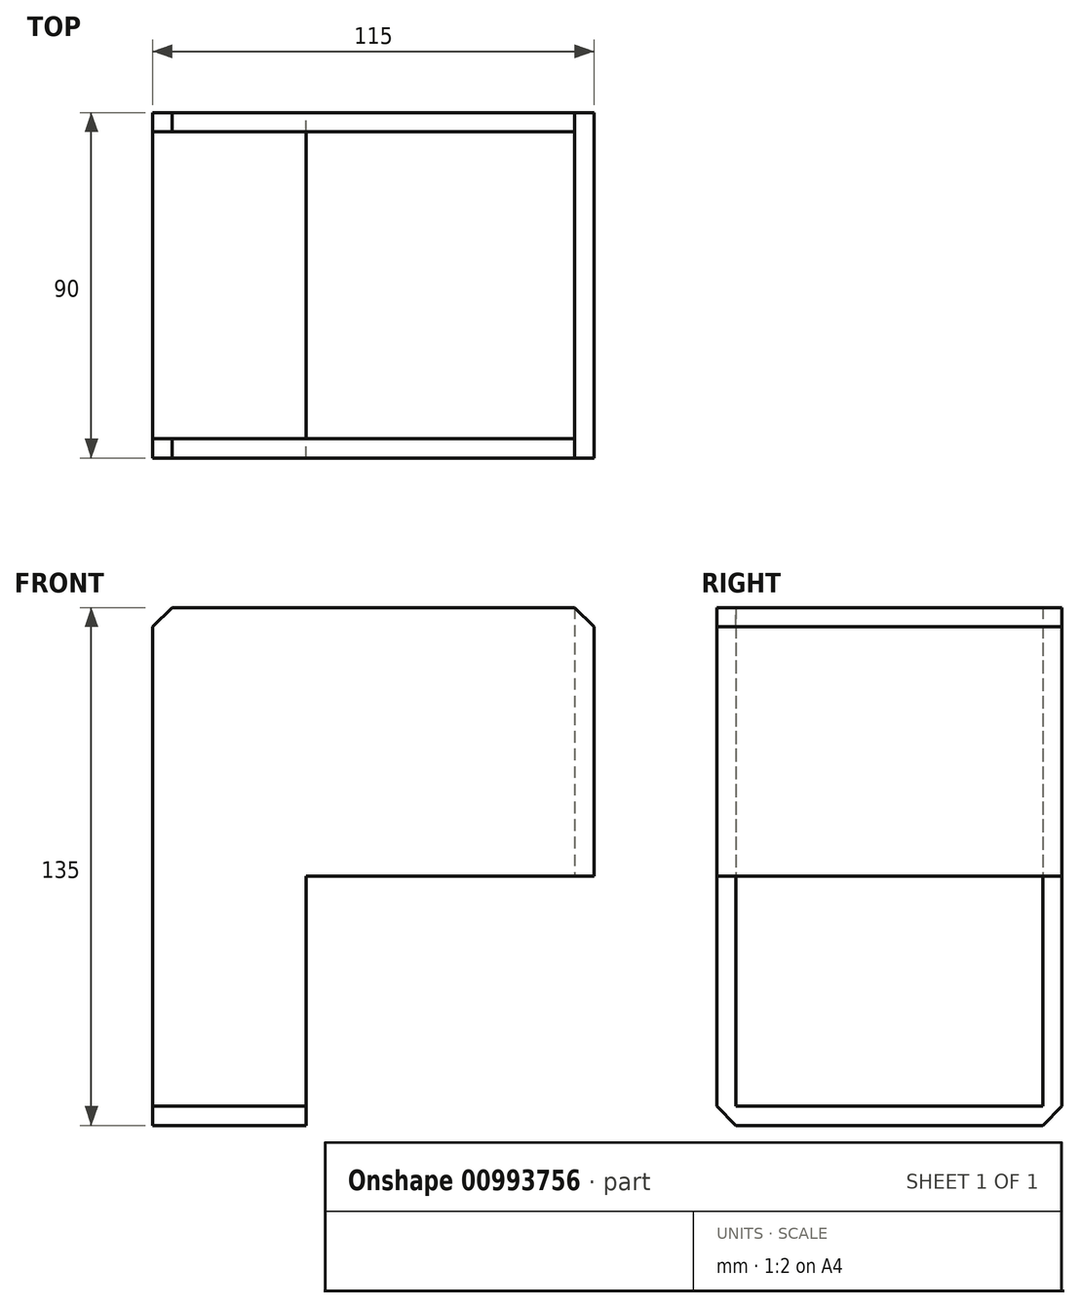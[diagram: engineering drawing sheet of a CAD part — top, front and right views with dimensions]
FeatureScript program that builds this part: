
annotation { "Feature Type Name" : "Feature", "Feature Type Description" : "" }
export const myFeature = defineFeature(function(context is Context, id is Id, definition is map)
    precondition{}
    {
        {
            var Q0;
            Q0=qCreatedBy(makeId("Right.planeOp"),FACE);
            var sketch = newSketch(context, id + "F0", { "sketchPlane" : qUnion([Q0])});
            skLineSegment(sketch, "E0.bottom", {"start": v(-45, 35) * mm, "end": v(45, 35) * mm});
            skLineSegment(sketch, "E0.top", {"start": v(-45, -35) * mm, "end": v(45, -35) * mm});
            skLineSegment(sketch, "E0.left", {"start": v(-45, 35) * mm, "end": v(-45, -35) * mm});
            skLineSegment(sketch, "E0.right", {"start": v(45, 35) * mm, "end": v(45, -35) * mm});
            skPoint(sketch, "E0.middle", {"position": v(0, 0) * mm});
            skSolve(sketch);
        }
        {
            var Q0;
            Q0=makeQuery(id+"F0.imprint","IMPRINT",FACE,{"disambiguationData":[TD([[makeQuery(id+"F0.imprint","IMPRINT",EDGE,{"derivedFrom":sQuery(id+"F0.wireOp",EDGE,"E0.bottom")}),-1.0]])]});
            extrude(context, id + "F1", {"entities" : qUnion([Q0]), "oppositeDirection" : true, "depth" : 5 * mm, "offsetDistance" : 25 * mm});
        }
        {
            var Q0;
            Q0=makeQuery(id+"F1.opExtrude","CAP_FACE",FACE,{"disambiguationData":[OSD([sQuery(id+"F0.wireOp",EDGE,"E0.bottom"),sQuery(id+"F0.wireOp",EDGE,"E0.top"),sQuery(id+"F0.wireOp",EDGE,"E0.left"),sQuery(id+"F0.wireOp",EDGE,"E0.right")])],"isStart":false});
            var sketch = newSketch(context, id + "F2", { "sketchPlane" : qUnion([Q0])});
            skLineSegment(sketch, "E1.bottom", {"start": v(-45, 35) * mm, "end": v(-40, 35) * mm});
            skLineSegment(sketch, "E1.top", {"start": v(-45, -35) * mm, "end": v(-40, -35) * mm});
            skLineSegment(sketch, "E1.left", {"start": v(-45, 35) * mm, "end": v(-45, -35) * mm});
            skLineSegment(sketch, "E1.right", {"start": v(-40, 35) * mm, "end": v(-40, -35) * mm});
            skLineSegment(sketch, "E2.bottom", {"start": v(45, 35) * mm, "end": v(40, 35) * mm});
            skLineSegment(sketch, "E2.top", {"start": v(45, -35) * mm, "end": v(40, -35) * mm});
            skLineSegment(sketch, "E2.left", {"start": v(45, 35) * mm, "end": v(45, -35) * mm});
            skLineSegment(sketch, "E2.right", {"start": v(40, 35) * mm, "end": v(40, -35) * mm});
            skSolve(sketch);
        }
        {
            var Q0;
            Q0 = qSketchRegion(id + "F2", true);
            extrude(context, id + "F3", {"entities" : qUnion([Q0]), "operationType" : NewBodyOperationType.ADD, "depth" : 110 * mm, "offsetDistance" : 25 * mm});
        }
        {
            var Q0;
            Q0=makeQuery(id+"F3.boolean.opBoolean","MERGE",FACE,{"derivedFrom":[makeQuery(id+"F1.opExtrude","SWEPT_FACE",FACE,{"disambiguationData":[OSD([sQuery(id+"F0.wireOp",EDGE,"E0.top")])]}),makeQuery(id+"F3.opExtrude","SWEPT_FACE",FACE,{"disambiguationData":[OSD([sQuery(id+"F2.wireOp",EDGE,"E1.top")])]}),makeQuery(id+"F3.opExtrude","SWEPT_FACE",FACE,{"disambiguationData":[OSD([sQuery(id+"F2.wireOp",EDGE,"E2.top")])]})]});
            var sketch = newSketch(context, id + "F4", { "sketchPlane" : qUnion([Q0])});
            skLineSegment(sketch, "E3.bottom", {"start": v(-115, 45) * mm, "end": v(-75, 45) * mm});
            skLineSegment(sketch, "E3.top", {"start": v(-115, 40) * mm, "end": v(-75, 40) * mm});
            skLineSegment(sketch, "E3.left", {"start": v(-115, 45) * mm, "end": v(-115, 40) * mm});
            skLineSegment(sketch, "E3.right", {"start": v(-75, 45) * mm, "end": v(-75, 40) * mm});
            skLineSegment(sketch, "E4.bottom", {"start": v(-115, -40) * mm, "end": v(-75, -40) * mm});
            skLineSegment(sketch, "E4.top", {"start": v(-115, -45) * mm, "end": v(-75, -45) * mm});
            skLineSegment(sketch, "E4.left", {"start": v(-115, -40) * mm, "end": v(-115, -45) * mm});
            skLineSegment(sketch, "E4.right", {"start": v(-75, -40) * mm, "end": v(-75, -45) * mm});
            skSolve(sketch);
        }
        {
            var Q0;
            Q0 = qSketchRegion(id + "F4", true);
            extrude(context, id + "F5", {"entities" : qUnion([Q0]), "operationType" : NewBodyOperationType.ADD, "depth" : 65 * mm, "offsetDistance" : 25 * mm});
        }
        {
            var Q0;
            Q0=makeQuery(id+"F5.boolean.opBoolean","MERGE",FACE,{"derivedFrom":[makeQuery(id+"F3.opExtrude","SWEPT_FACE",FACE,{"disambiguationData":[OSD([sQuery(id+"F2.wireOp",EDGE,"E2.right")])]}),makeQuery(id+"F5.opExtrude","SWEPT_FACE",FACE,{"disambiguationData":[OSD([sQuery(id+"F4.wireOp",EDGE,"E3.top")])]})]});
            var sketch = newSketch(context, id + "F6", { "sketchPlane" : qUnion([Q0])});
            skLineSegment(sketch, "E5.bottom", {"start": v(75, -100) * mm, "end": v(115, -100) * mm});
            skLineSegment(sketch, "E5.top", {"start": v(75, -95) * mm, "end": v(115, -95) * mm});
            skLineSegment(sketch, "E5.left", {"start": v(75, -100) * mm, "end": v(75, -95) * mm});
            skLineSegment(sketch, "E5.right", {"start": v(115, -100) * mm, "end": v(115, -95) * mm});
            skSolve(sketch);
        }
        {
            var Q0;
            Q0 = qSketchRegion(id + "F6", true);
            extrude(context, id + "F7", {"entities" : qUnion([Q0]), "operationType" : NewBodyOperationType.ADD, "endBound" : BoundingType.UP_TO_NEXT, "depth" : 25 * mm, "offsetDistance" : 25 * mm});
        }
        {
            var Q0;
            Q0=makeQuery(id+"F1.opExtrude","CAP_EDGE",EDGE,{"disambiguationData":[OSD([sQuery(id+"F0.wireOp",EDGE,"E0.bottom")])],"isStart":true});
            var Q1;
            Q1=makeQuery(id+"F3.opExtrude","CAP_EDGE",EDGE,{"disambiguationData":[OSD([sQuery(id+"F2.wireOp",EDGE,"E1.bottom")])],"isStart":false});
            var Q2;
            Q2=makeQuery(id+"F3.opExtrude","CAP_EDGE",EDGE,{"disambiguationData":[OSD([sQuery(id+"F2.wireOp",EDGE,"E2.bottom")])],"isStart":false});
            var Q3;
            Q3=makeQuery(id+"F5.opExtrude","CAP_EDGE",EDGE,{"disambiguationData":[OSD([sQuery(id+"F4.wireOp",EDGE,"E3.bottom")])],"isStart":false});
            var Q4;
            Q4=makeQuery(id+"F7.opExtrude","CAP_EDGE",EDGE,{"disambiguationData":[OSD([sQuery(id+"F6.wireOp",EDGE,"E5.top")])],"isStart":true});
            var Q5;
            Q5=makeQuery(id+"F7.opExtrude","CAP_EDGE",EDGE,{"disambiguationData":[OSD([sQuery(id+"F6.wireOp",EDGE,"E5.top")])],"isStart":false});
            var Q6;
            Q6=makeQuery(id+"F5.opExtrude","CAP_EDGE",EDGE,{"disambiguationData":[OSD([sQuery(id+"F4.wireOp",EDGE,"E4.top")])],"isStart":false});
            chamfer(context, id + "F8", {"entities" : qUnion([Q0, Q1, Q2, Q3, Q4, Q5, Q6]), "width" : 5 * mm, "tangentPropagation" : true});
        }
    });
